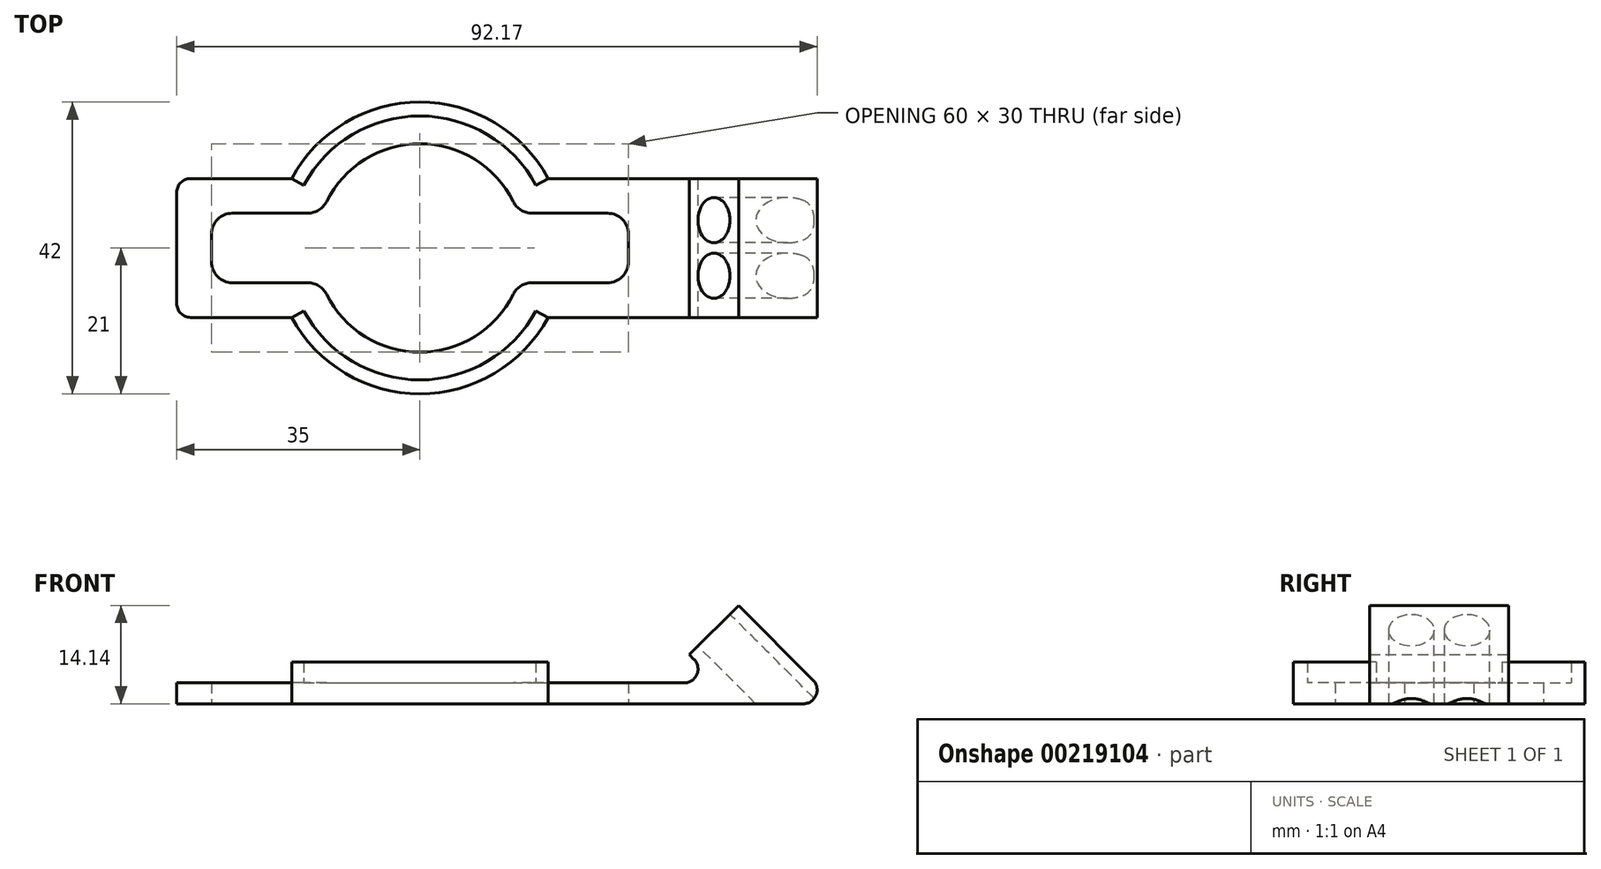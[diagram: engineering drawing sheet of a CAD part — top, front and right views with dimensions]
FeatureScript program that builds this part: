
annotation { "Feature Type Name" : "Feature", "Feature Type Description" : "" }
export const myFeature = defineFeature(function(context is Context, id is Id, definition is map)
    precondition{}
    {
        {
            var Q0;
            Q0=qCreatedBy(makeId("Front.planeOp"),FACE);
            var sketch = newSketch(context, id + "F0", { "sketchPlane" : qUnion([Q0])});
            skLineSegment(sketch, "E0", {"start": v(0, 0) * mm, "end": v(20.17, 0) * mm});
            skLineSegment(sketch, "E1", {"start": v(21.59, 3.41) * mm, "end": v(10.86, 14.14) * mm});
            skLineSegment(sketch, "E2", {"start": v(10.86, 14.14) * mm, "end": v(3.79, 7.07) * mm});
            skLineSegment(sketch, "E3", {"start": v(3.79, 7.07) * mm, "end": v(4.44, 6.41) * mm});
            skLineSegment(sketch, "E4", {"start": v(3.03, 3) * mm, "end": v(0, 3) * mm});
            skLineSegment(sketch, "E5", {"start": v(0, 3) * mm, "end": v(0, 0) * mm});
            skPoint(sketch, "E6.visualSharp", {"position": v(25, 0) * mm});
            skArc(sketch, "E6.filletArc", {"start": v(20.17, 0) * mm, "mid": v(22.02, 1.23) * mm, "end": v(21.59, 3.41) * mm});
            skPoint(sketch, "E7.visualSharp", {"position": v(7.86, 3) * mm});
            skArc(sketch, "E7.filletArc", {"start": v(3.03, 3) * mm, "mid": v(4.88, 4.23) * mm, "end": v(4.44, 6.41) * mm});
            skSolve(sketch);
        }
        {
            var Q0;
            Q0=qSketchRegion(id+"F0",true);
            extrude(context, id + "F1", {"entities" : qUnion([Q0]), "endBound" : BoundingType.SYMMETRIC, "depth" : 20 * mm});
        }
        {
            var Q0;
            Q0=makeQuery(id+"F1.opExtrude","SWEPT_FACE",FACE,{"disambiguationData":[OSD([sQuery(id+"F0.wireOp",EDGE,"E2")])]});
            var sketch = newSketch(context, id + "F2", { "sketchPlane" : qUnion([Q0])});
            skLineSegment(sketch, "E8", {"start": v(0, 7.68) * mm, "end": v(0, 17.68) * mm, "construction": true});
            skLineSegment(sketch, "E9", {"start": v(0, 12.68) * mm, "end": v(-4, 12.68) * mm, "construction": true});
            skCircle(sketch, "E10", {"center": v(-4, 12.68) * mm, "radius": 3.25 * mm});
            skCircle(sketch, "E11.MirrorC", {"center": v(4, 12.68) * mm, "radius": 3.25 * mm});
            skSolve(sketch);
        }
        {
            var Q0;
            Q0=qSketchRegion(id+"F2",true);
            extrude(context, id + "F3", {"entities" : qUnion([Q0]), "operationType" : NewBodyOperationType.REMOVE, "oppositeDirection" : true, "depth" : 25 * mm});
        }
        {
            var Q0;
            Q0=qCreatedBy(makeId("Top.planeOp"),FACE);
            var sketch = newSketch(context, id + "F4", { "sketchPlane" : qUnion([Q0])});
            skLineSegment(sketch, "E12.bottom", {"start": v(0, 10) * mm, "end": v(-16.53, 10) * mm});
            skLineSegment(sketch, "E12.top", {"start": v(0, -10) * mm, "end": v(-16.53, -10) * mm});
            skLineSegment(sketch, "E12.left", {"start": v(0, 10) * mm, "end": v(0, -10) * mm});
            skLineSegment(sketch, "E12.right", {"start": v(-70, 8) * mm, "end": v(-70, -8) * mm});
            skPoint(sketch, "E13.visualSharp", {"position": v(-70, -10) * mm});
            skArc(sketch, "E13.filletArc", {"start": v(-70, -8) * mm, "mid": v(-69.41, -9.41) * mm, "end": v(-68, -10) * mm});
            skPoint(sketch, "E14.visualSharp", {"position": v(-70, 10) * mm});
            skArc(sketch, "E14.filletArc", {"start": v(-68, 10) * mm, "mid": v(-69.41, 9.41) * mm, "end": v(-70, 8) * mm});
            skCircle(sketch, "E15", {"center": v(-35, 0) * mm, "radius": 19 * mm, "construction": true});
            skArc(sketch, "E16", {"start": v(-53.47, -10) * mm, "mid": v(-35, -21) * mm, "end": v(-16.53, -10) * mm});
            skLineSegment(sketch, "E17.trimOffspring", {"start": v(-53.47, 10) * mm, "end": v(-68, 10) * mm});
            skLineSegment(sketch, "E18.trimOffspring", {"start": v(-53.47, -10) * mm, "end": v(-68, -10) * mm});
            skArc(sketch, "E19.trimOffspring", {"start": v(-16.53, 10) * mm, "mid": v(-35, 21) * mm, "end": v(-53.47, 10) * mm});
            skArc(sketch, "E20", {"start": v(-48.44, -6.67) * mm, "mid": v(-35, -15) * mm, "end": v(-21.56, -6.67) * mm});
            skLineSegment(sketch, "E21.bottom", {"start": v(-8, 5) * mm, "end": v(-18.88, 5) * mm});
            skLineSegment(sketch, "E21.top", {"start": v(-8, -5) * mm, "end": v(-18.88, -5) * mm});
            skLineSegment(sketch, "E21.left", {"start": v(-5, 2) * mm, "end": v(-5, -2) * mm});
            skLineSegment(sketch, "E21.right", {"start": v(-65, 2) * mm, "end": v(-65, -2) * mm});
            skArc(sketch, "E22.trimOffspring", {"start": v(-21.56, 6.67) * mm, "mid": v(-35, 15) * mm, "end": v(-48.44, 6.67) * mm});
            skLineSegment(sketch, "E23.trimOffspring", {"start": v(-51.12, 5) * mm, "end": v(-62, 5) * mm});
            skLineSegment(sketch, "E24.trimOffspring", {"start": v(-51.12, -5) * mm, "end": v(-62, -5) * mm});
            skPoint(sketch, "E25.visualSharp", {"position": v(-49.14, 5) * mm});
            skArc(sketch, "E25.filletArc", {"start": v(-51.12, 5) * mm, "mid": v(-49.54, 5.45) * mm, "end": v(-48.44, 6.67) * mm});
            skPoint(sketch, "E26.visualSharp", {"position": v(-20.86, 5) * mm});
            skArc(sketch, "E26.filletArc", {"start": v(-21.56, 6.67) * mm, "mid": v(-20.46, 5.45) * mm, "end": v(-18.88, 5) * mm});
            skPoint(sketch, "E27.visualSharp", {"position": v(-5, 5) * mm});
            skArc(sketch, "E27.filletArc", {"start": v(-5, 2) * mm, "mid": v(-5.88, 4.12) * mm, "end": v(-8, 5) * mm});
            skPoint(sketch, "E28.visualSharp", {"position": v(-5, -5) * mm});
            skArc(sketch, "E28.filletArc", {"start": v(-8, -5) * mm, "mid": v(-5.88, -4.12) * mm, "end": v(-5, -2) * mm});
            skPoint(sketch, "E29.visualSharp", {"position": v(-20.86, -5) * mm});
            skArc(sketch, "E29.filletArc", {"start": v(-18.88, -5) * mm, "mid": v(-20.46, -5.45) * mm, "end": v(-21.56, -6.67) * mm});
            skPoint(sketch, "E30.visualSharp", {"position": v(-49.14, -5) * mm});
            skArc(sketch, "E30.filletArc", {"start": v(-48.44, -6.67) * mm, "mid": v(-49.54, -5.45) * mm, "end": v(-51.12, -5) * mm});
            skPoint(sketch, "E31.visualSharp", {"position": v(-65, -5) * mm});
            skArc(sketch, "E31.filletArc", {"start": v(-65, -2) * mm, "mid": v(-64.12, -4.12) * mm, "end": v(-62, -5) * mm});
            skPoint(sketch, "E32.visualSharp", {"position": v(-65, 5) * mm});
            skArc(sketch, "E32.filletArc", {"start": v(-62, 5) * mm, "mid": v(-64.12, 4.12) * mm, "end": v(-65, 2) * mm});
            skSolve(sketch);
        }
        {
            var Q0;
            Q0=makeQuery(id+"F4.imprint","IMPRINT",FACE,{"disambiguationData":[TD([[makeQuery(id+"F4.imprint","IMPRINT",EDGE,{"derivedFrom":sQuery(id+"F4.wireOp",EDGE,"E12.bottom")}),1.0]])]});
            extrude(context, id + "F5", {"entities" : qUnion([Q0]), "operationType" : NewBodyOperationType.ADD, "depth" : 3 * mm});
        }
        {
            var Q0;
            Q0=makeQuery(id+"F5.boolean.opBoolean","MERGE",FACE,{"derivedFrom":[makeQuery(id+"F1.opExtrude","SWEPT_FACE",FACE,{"disambiguationData":[OSD([sQuery(id+"F0.wireOp",EDGE,"E4")])]}),makeQuery(id+"F5.opExtrude","CAP_FACE",FACE,{"disambiguationData":[OSD([sQuery(id+"F4.wireOp",EDGE,"E12.bottom"),sQuery(id+"F4.wireOp",EDGE,"E12.top"),sQuery(id+"F4.wireOp",EDGE,"E12.left"),sQuery(id+"F4.wireOp",EDGE,"E12.right"),sQuery(id+"F4.wireOp",EDGE,"E13.filletArc"),sQuery(id+"F4.wireOp",EDGE,"E14.filletArc"),sQuery(id+"F4.wireOp",EDGE,"E16"),sQuery(id+"F4.wireOp",EDGE,"E17.trimOffspring"),sQuery(id+"F4.wireOp",EDGE,"E18.trimOffspring"),sQuery(id+"F4.wireOp",EDGE,"E19.trimOffspring")])],"isStart":false})]});
            var sketch = newSketch(context, id + "F6", { "sketchPlane" : qUnion([Q0])});
            skArc(sketch, "E33", {"start": v(-18.3, 9.05) * mm, "mid": v(-35, 19) * mm, "end": v(-51.7, 9.05) * mm});
            skLineSegment(sketch, "E34", {"start": v(-51.7, 9.05) * mm, "end": v(-53.47, 10) * mm});
            skLineSegment(sketch, "E35", {"start": v(-18.3, 9.05) * mm, "end": v(-16.53, 10) * mm});
            skLineSegment(sketch, "E36", {"start": v(-35, 0) * mm, "end": v(0, 0) * mm, "construction": true});
            skArc(sketch, "E37", {"start": v(-16.53, 10) * mm, "mid": v(-35, 21) * mm, "end": v(-53.47, 10) * mm});
            skArc(sketch, "E38.MirrorCS", {"start": v(-18.3, -9.05) * mm, "mid": v(-35, -19) * mm, "end": v(-51.7, -9.05) * mm});
            skLineSegment(sketch, "E39.MirrorCS", {"start": v(-18.3, -9.05) * mm, "end": v(-16.53, -10) * mm});
            skLineSegment(sketch, "E40.MirrorCS", {"start": v(-51.7, -9.05) * mm, "end": v(-53.47, -10) * mm});
            skArc(sketch, "E41.MirrorCS", {"start": v(-16.53, -10) * mm, "mid": v(-35, -21) * mm, "end": v(-53.47, -10) * mm});
            skSolve(sketch);
        }
        {
            var Q0;
            Q0 = qSketchRegion(id + "F6", true);
            extrude(context, id + "F7", {"entities" : qUnion([Q0]), "operationType" : NewBodyOperationType.ADD, "depth" : 3 * mm});
        }
    });
